# Revit family: MUCOR-48-H11-I
name_source: partatom
category: Equipos mecánicos
units: mm (PartAtom-declared; Revit-internal decimal feet)

## family parameters
Compartido = No
Corte con vacíos al cargar = No
Cota de conector redondo = Diámetro de uso
Número OmniClass = 23.75.00.00
Punto de cálculo de habitación = No
Se basa en plano de trabajo = No
Siempre vertical = Sí
Tipo de pieza = Normal
Título OmniClass = Climate Control (HVAC)

## types (1)
- MUCOR-48-H11-I
    Air  Flow = 2413/2222/2027 m3/h
    Casing color = SB2403
    Cooling Capacity = 14068.000 W
    Cooling Power Input = 4950 W
    Depth = 456.000 mm
    Descripción = Floor standing
    Drain piping = 16.000 mm
    Elevación por defecto = 0.000 mm
    Gas = R32
    Gas pipe = 15.900 mm
    Heating Capacity = 16120.000 W
    Heating Power Input = 5100 W
    Height = 1935.000 mm
    Installation = Indoor installation
    Liquid pipe = 9.520 mm
    Maximum Fuse Amps = 10 A
    Modelo = MUCOR-48-H11-I
    Net Weight = 59.00 kg
    Power supply = 1 phase, 220-240V, 50Hz
    Width = 629.000 mm
    clearance access behind = 50.000 mm
    clearance access front = 2000.000 mm
    clearance access left = 500.000 mm
    clearance access right = 500.000 mm
    clearance access up = 300.000 mm
